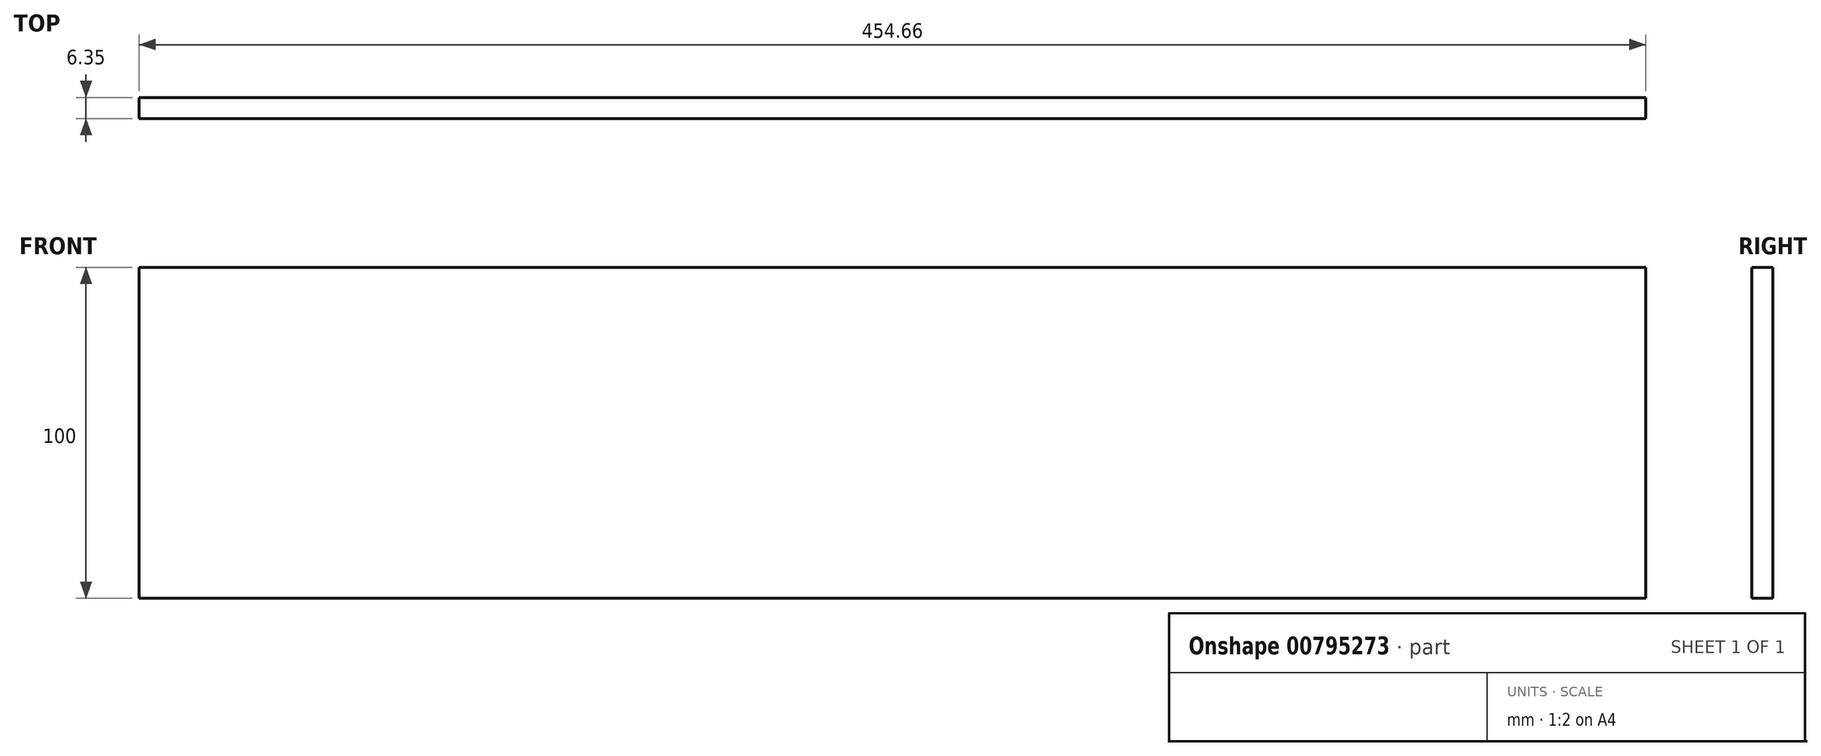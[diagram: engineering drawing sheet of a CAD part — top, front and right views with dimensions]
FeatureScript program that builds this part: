
annotation { "Feature Type Name" : "Feature", "Feature Type Description" : "" }
export const myFeature = defineFeature(function(context is Context, id is Id, definition is map)
    precondition{}
    {
        {
            var Q0;
            Q0=qCreatedBy(makeId("Front.planeOp"),FACE);
            var sketch = newSketch(context, id + "F0", { "sketchPlane" : qUnion([Q0])});
            skLineSegment(sketch, "E0.bottom", {"start": v(227.33, -50) * mm, "end": v(-227.33, -50) * mm});
            skLineSegment(sketch, "E0.top", {"start": v(227.33, 50) * mm, "end": v(-227.33, 50) * mm});
            skLineSegment(sketch, "E0.left", {"start": v(227.33, -50) * mm, "end": v(227.33, 50) * mm});
            skLineSegment(sketch, "E0.right", {"start": v(-227.33, -50) * mm, "end": v(-227.33, 50) * mm});
            skPoint(sketch, "E0.middle", {"position": v(0, 0) * mm});
            skSolve(sketch);
        }
        {
            var Q0;
            Q0=makeQuery(id+"F0.imprint","IMPRINT",FACE,{"disambiguationData":[TD([[makeQuery(id+"F0.imprint","IMPRINT",EDGE,{"derivedFrom":sQuery(id+"F0.wireOp",EDGE,"E0.bottom")}),-1.0]])]});
            extrude(context, id + "F1", {"entities" : qUnion([Q0]), "depth" : 6.35 * mm, "offsetDistance" : 25.4 * mm});
        }
    });
